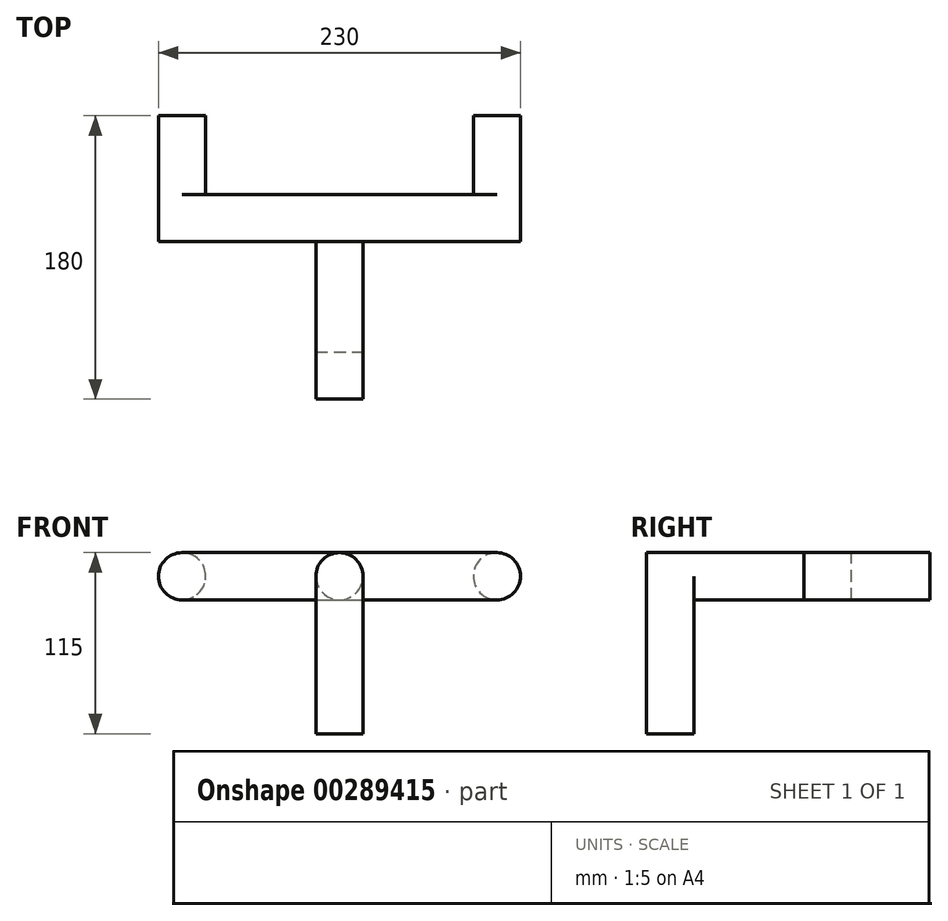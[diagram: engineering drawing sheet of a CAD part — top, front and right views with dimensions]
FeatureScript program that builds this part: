
annotation { "Feature Type Name" : "Feature", "Feature Type Description" : "" }
export const myFeature = defineFeature(function(context is Context, id is Id, definition is map)
    precondition{}
    {
        {
            var Q0;
            Q0=qCreatedBy(makeId("Front.planeOp"),FACE);
            var sketch = newSketch(context, id + "F0", { "sketchPlane" : qUnion([Q0])});
            skCircle(sketch, "E0", {"center": v(-100, 0) * mm, "radius": 15 * mm});
            skCircle(sketch, "E1", {"center": v(100, 0) * mm, "radius": 15 * mm});
            skLineSegment(sketch, "E2.bottom", {"start": v(-100, 15) * mm, "end": v(100, 15) * mm});
            skLineSegment(sketch, "E2.top", {"start": v(-100, -15) * mm, "end": v(100, -15) * mm});
            skLineSegment(sketch, "E2.left", {"start": v(-100, 15) * mm, "end": v(-100, -15) * mm});
            skLineSegment(sketch, "E2.right", {"start": v(100, 15) * mm, "end": v(100, -15) * mm});
            skSolve(sketch);
        }
        {
            var Q0;
            Q0=makeQuery(id+"F0.imprint","IMPRINT",FACE,{"disambiguationData":[TD([[makeQuery(id+"F0.imprint","IMPRINT",EDGE,{"derivedFrom":sQuery(id+"F0.wireOp",EDGE,"E0")}),1.0]])]});
            var Q1;
            Q1=makeQuery(id+"F0.imprint","IMPRINT",FACE,{"disambiguationData":[TD([[makeQuery(id+"F0.imprint","IMPRINT",EDGE,{"derivedFrom":sQuery(id+"F0.wireOp",EDGE,"E1")}),1.0]])]});
            extrude(context, id + "F1", {"entities" : qUnion([Q0, Q1]), "oppositeDirection" : true, "depth" : 50 * mm});
        }
        {
            var Q0;
            {var subQ0=sQuery(id+"F0.wireOp",EDGE,"E2.left");Q0=makeQuery(id+"F0.imprint","IMPRINT",FACE,{"disambiguationData":[TD([[makeQuery(id+"F0.imprint","IMPRINT",EDGE,{"derivedFrom":subQ0}),-1.0]])]});}
            var Q1;
            {var subQ0=sQuery(id+"F0.wireOp",EDGE,"E2.left");Q1=makeQuery(id+"F0.imprint","IMPRINT",FACE,{"disambiguationData":[TD([[makeQuery(id+"F0.imprint","IMPRINT",EDGE,{"derivedFrom":subQ0}),1.0]])]});}
            var Q2;
            {var subQ0=sQuery(id+"F0.wireOp",EDGE,"E2.right");Q2=makeQuery(id+"F0.imprint","IMPRINT",FACE,{"disambiguationData":[TD([[makeQuery(id+"F0.imprint","IMPRINT",EDGE,{"derivedFrom":subQ0}),-1.0]])]});}
            var Q3;
            {var subQ0=sQuery(id+"F0.wireOp",EDGE,"E2.right");Q3=makeQuery(id+"F0.imprint","IMPRINT",FACE,{"disambiguationData":[TD([[makeQuery(id+"F0.imprint","IMPRINT",EDGE,{"derivedFrom":subQ0}),1.0]])]});}
            extrude(context, id + "F2", {"entities" : qUnion([Q0, Q1, Q2, Q3]), "oppositeDirection" : true, "depth" : 50 * mm});
        }
        {
            var Q0;
            {var subQ0=sQuery(id+"F0.wireOp",EDGE,"E2.bottom");Q0=makeQuery(id+"F0.imprint","IMPRINT",FACE,{"disambiguationData":[TD([[makeQuery(id+"F0.imprint","IMPRINT",EDGE,{"derivedFrom":subQ0}),-1.0]])]});}
            var Q1;
            {var subQ0=sQuery(id+"F0.wireOp",EDGE,"E2.left");Q1=makeQuery(id+"F0.imprint","IMPRINT",FACE,{"disambiguationData":[TD([[makeQuery(id+"F0.imprint","IMPRINT",EDGE,{"derivedFrom":subQ0}),-1.0]])]});}
            var Q2;
            {var subQ0=sQuery(id+"F0.wireOp",EDGE,"E2.left");Q2=makeQuery(id+"F0.imprint","IMPRINT",FACE,{"disambiguationData":[TD([[makeQuery(id+"F0.imprint","IMPRINT",EDGE,{"derivedFrom":subQ0}),1.0]])]});}
            var Q3;
            {var subQ0=sQuery(id+"F0.wireOp",EDGE,"E2.right");Q3=makeQuery(id+"F0.imprint","IMPRINT",FACE,{"disambiguationData":[TD([[makeQuery(id+"F0.imprint","IMPRINT",EDGE,{"derivedFrom":subQ0}),-1.0]])]});}
            var Q4;
            {var subQ0=sQuery(id+"F0.wireOp",EDGE,"E2.right");Q4=makeQuery(id+"F0.imprint","IMPRINT",FACE,{"disambiguationData":[TD([[makeQuery(id+"F0.imprint","IMPRINT",EDGE,{"derivedFrom":subQ0}),1.0]])]});}
            extrude(context, id + "F3", {"entities" : qUnion([Q0, Q1, Q2, Q3, Q4]), "depth" : 30 * mm});
        }
        {
            var Q0;
            Q0=makeQuery(id+"F3.opExtrude","CAP_FACE",FACE,{"disambiguationData":[OSD([sQuery(id+"F0.wireOp",EDGE,"E2.bottom"),sQuery(id+"F0.wireOp",EDGE,"E2.top"),sQuery(id+"F0.wireOp",EDGE,"E0"),sQuery(id+"F0.wireOp",EDGE,"E1")])],"isStart":false});
            var sketch = newSketch(context, id + "F4", { "sketchPlane" : qUnion([Q0])});
            skCircle(sketch, "E3", {"center": v(0, 0) * mm, "radius": 15 * mm});
            skSolve(sketch);
        }
        {
            var Q0;
            {var subQ0=sQuery(id+"F4.wireOp",EDGE,"E3");var subQ1=makeQuery(id+"F4.imprint","INTERSECT",VERTEX,{"derivedFrom":[makeQuery(id+"F3.opExtrude","CAP_EDGE",EDGE,{"disambiguationData":[OSD([sQuery(id+"F0.wireOp",EDGE,"E2.bottom")])],"isStart":false}),subQ0]});Q0=makeQuery(id+"F4.imprint","IMPRINT",FACE,{"disambiguationData":[TD([[makeQuery(id+"F4.imprint","IMPRINT",EDGE,{"disambiguationData":[TD([[subQ1,-1.0]])],"derivedFrom":subQ0}),1.0]])]});}
            extrude(context, id + "F5", {"entities" : qUnion([Q0]), "operationType" : NewBodyOperationType.ADD, "depth" : 100 * mm});
        }
        {
            var Q0;
            Q0=makeQuery(id+"F2.opExtrude","SWEPT_BODY",BODY,{"disambiguationData":[OSD([sQuery(id+"F0.wireOp",EDGE,"E0")])]});
            deleteBodies(context, id + "F6", {"entities" : qUnion([Q0])});
        }
        {
            var Q0;
            Q0=makeQuery(id+"F2.opExtrude","SWEPT_BODY",BODY,{"disambiguationData":[OSD([sQuery(id+"F0.wireOp",EDGE,"E1")])]});
            deleteBodies(context, id + "F7", {"entities" : qUnion([Q0])});
        }
        {
            var Q0;
            Q0=makeQuery(id+"F3.opExtrude","CAP_FACE",FACE,{"disambiguationData":[OSD([sQuery(id+"F0.wireOp",EDGE,"E2.bottom"),sQuery(id+"F0.wireOp",EDGE,"E2.top"),sQuery(id+"F0.wireOp",EDGE,"E0"),sQuery(id+"F0.wireOp",EDGE,"E1")])],"isStart":true});
            var sketch = newSketch(context, id + "F8", { "sketchPlane" : qUnion([Q0])});
            skCircle(sketch, "E4", {"center": v(100, 0) * mm, "radius": 15 * mm});
            skCircle(sketch, "E5", {"center": v(-100, 0) * mm, "radius": 15 * mm});
            skSolve(sketch);
        }
        {
            var Q0;
            Q0 = qSketchRegion(id + "F8", true);
            extrude(context, id + "F9", {"entities" : qUnion([Q0]), "operationType" : NewBodyOperationType.ADD, "depth" : 50 * mm});
        }
        {
            var Q0;
            Q0=qCreatedBy(makeId("Top.planeOp"),FACE);
            var sketch = newSketch(context, id + "F10", { "sketchPlane" : qUnion([Q0])});
            skLineSegment(sketch, "E6", {"start": v(0, 0) * mm, "end": v(0, -130) * mm});
            skLineSegment(sketch, "E7", {"start": v(0, -130) * mm, "end": v(-15, -130) * mm});
            skLineSegment(sketch, "E8", {"start": v(-15, -130) * mm, "end": v(-15, -100) * mm});
            skLineSegment(sketch, "E9.bottom", {"start": v(-15, -130) * mm, "end": v(15, -130) * mm});
            skLineSegment(sketch, "E9.top", {"start": v(-15, -100) * mm, "end": v(15, -100) * mm});
            skLineSegment(sketch, "E9.right", {"start": v(15, -130) * mm, "end": v(15, -100) * mm});
            skSolve(sketch);
        }
        {
            var Q0;
            Q0 = qSketchRegion(id + "F10", true);
            extrude(context, id + "F11", {"entities" : qUnion([Q0]), "operationType" : NewBodyOperationType.ADD, "oppositeDirection" : true, "depth" : 100 * mm});
        }
    });
